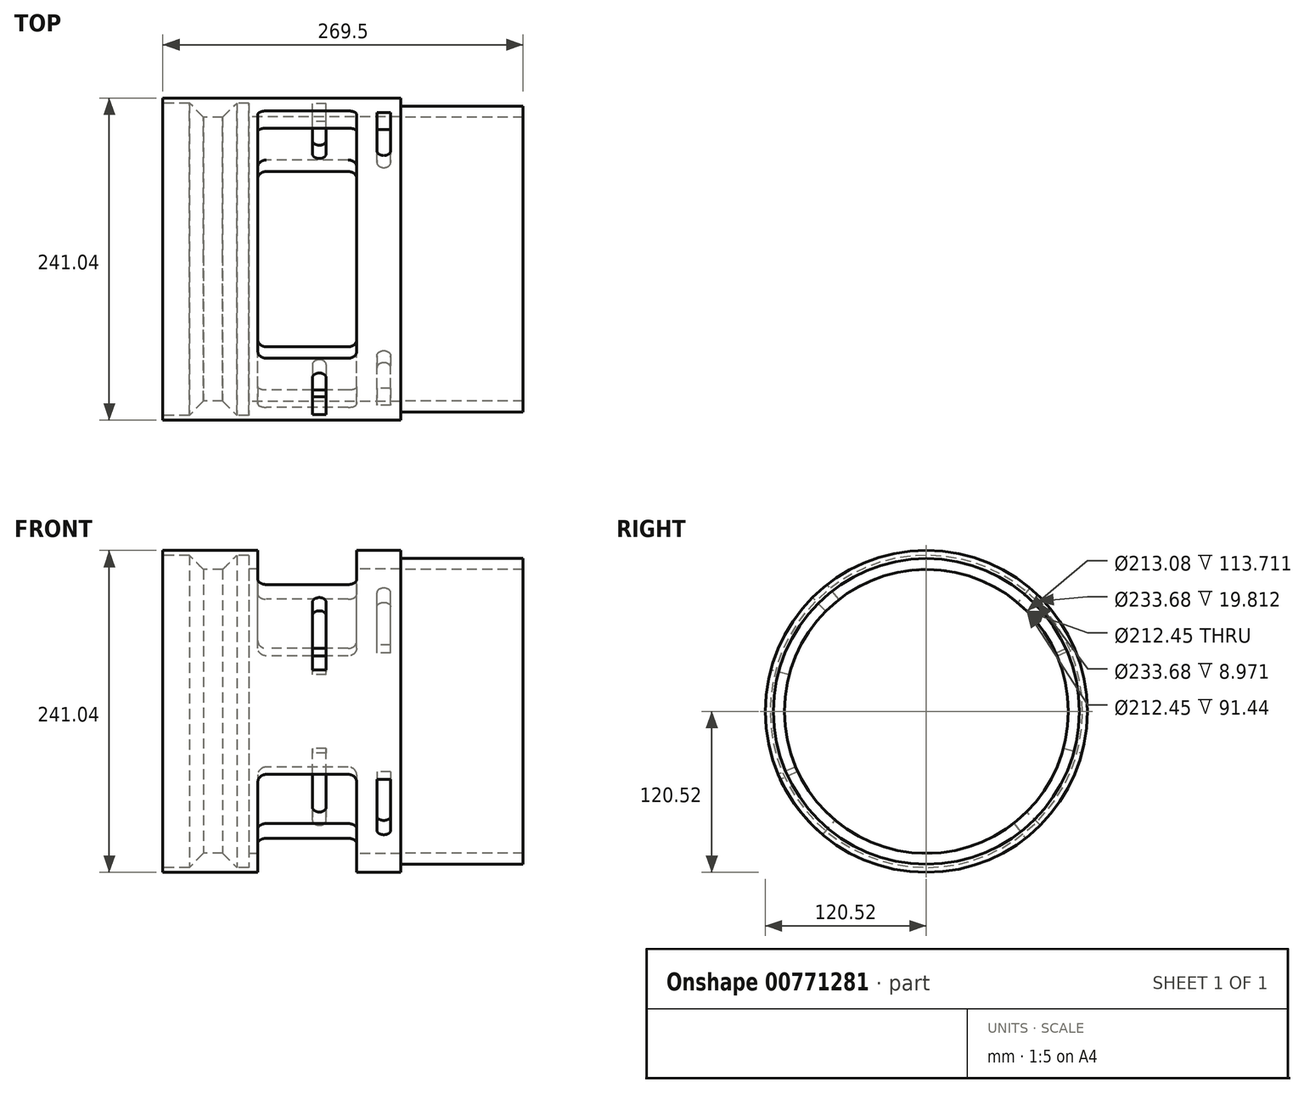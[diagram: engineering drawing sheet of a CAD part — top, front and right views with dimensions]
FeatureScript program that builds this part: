
annotation { "Feature Type Name" : "Feature", "Feature Type Description" : "" }
export const myFeature = defineFeature(function(context is Context, id is Id, definition is map)
    precondition{}
    {
        {
            var Q0;
            Q0=qCreatedBy(makeId("Front.planeOp"),FACE);
            var sketch = newSketch(context, id + "F0", { "sketchPlane" : qUnion([Q0])});
            skLineSegment(sketch, "E0", {"start": v(-108.05, 0) * mm, "end": v(161.45, 0) * mm, "construction": true});
            skLineSegment(sketch, "E1", {"start": v(-77.62, 106.22) * mm, "end": v(-63.3, 106.22) * mm});
            skLineSegment(sketch, "E2", {"start": v(-108.05, 116.84) * mm, "end": v(-108.05, 120.52) * mm});
            skLineSegment(sketch, "E3", {"start": v(-108.05, 120.52) * mm, "end": v(70, 120.52) * mm});
            skLineSegment(sketch, "E4", {"start": v(161.45, 114.44) * mm, "end": v(161.45, 106.22) * mm});
            skLineSegment(sketch, "E5", {"start": v(-108.05, 116.84) * mm, "end": v(-88.24, 116.84) * mm});
            skLineSegment(sketch, "E6", {"start": v(-88.24, 116.84) * mm, "end": v(-77.62, 106.22) * mm});
            skPoint(sketch, "E7.orphan", {"position": v(-108.05, 106.22) * mm});
            skLineSegment(sketch, "E8", {"start": v(70, 120.52) * mm, "end": v(70, 114.44) * mm});
            skLineSegment(sketch, "E9", {"start": v(70, 114.44) * mm, "end": v(161.45, 114.44) * mm});
            skLineSegment(sketch, "E10", {"start": v(-63.63, 105.89) * mm, "end": v(-52.68, 116.84) * mm});
            skLineSegment(sketch, "E11", {"start": v(-52.68, 116.84) * mm, "end": v(-43.7, 116.84) * mm});
            skLineSegment(sketch, "E12", {"start": v(-43.7, 116.84) * mm, "end": v(-43.7, 106.54) * mm});
            skLineSegment(sketch, "E13", {"start": v(-43.7, 106.54) * mm, "end": v(70, 106.54) * mm});
            skLineSegment(sketch, "E14", {"start": v(70, 106.54) * mm, "end": v(70, 106.22) * mm});
            skLineSegment(sketch, "E15.trimOffspring", {"start": v(70, 106.22) * mm, "end": v(161.45, 106.22) * mm});
            skSolve(sketch);
        }
        {
            var Q0;
            Q0 = qSketchRegion(id + "F0", true);
            var Q1;
            Q1=sQuery(id+"F0.wireOp",EDGE,"E0");
            revolve(context, id + "F1", {"surfaceOperationType" : NewSurfaceOperationType.NEW, "entities" : qUnion([Q0]), "axis" : qUnion([Q1]), "revolveType" : RevolveType.FULL});
        }
        {
            var Q0;
            Q0=qCreatedBy(makeId("Right.planeOp"),FACE);
            var sketch = newSketch(context, id + "F2", { "sketchPlane" : qUnion([Q0])});
            skLineSegment(sketch, "E16", {"start": v(0, 0) * mm, "end": v(-212.72, 0) * mm, "construction": true});
            skLineSegment(sketch, "E17", {"start": v(-60.07, 76.88) * mm, "end": v(-79.52, 101.78) * mm});
            skLineSegment(sketch, "E18", {"start": v(89.81, 38.12) * mm, "end": v(118.89, 50.47) * mm});
            skArc(sketch, "E19", {"start": v(89.81, 38.12) * mm, "mid": v(24.43, 94.46) * mm, "end": v(-60.07, 76.88) * mm});
            skArc(sketch, "E20", {"start": v(118.89, 50.47) * mm, "mid": v(32.34, 125.04) * mm, "end": v(-79.52, 101.78) * mm});
            skLineSegment(sketch, "E21", {"start": v(-89.81, -38.12) * mm, "end": v(-118.89, -50.47) * mm});
            skLineSegment(sketch, "E22", {"start": v(60.07, -76.88) * mm, "end": v(79.52, -101.78) * mm});
            skArc(sketch, "E23.trimOffspring", {"start": v(-89.81, -38.12) * mm, "mid": v(-24.43, -94.46) * mm, "end": v(60.07, -76.88) * mm});
            skArc(sketch, "E24.trimOffspring", {"start": v(-118.89, -50.47) * mm, "mid": v(-32.34, -125.04) * mm, "end": v(79.52, -101.78) * mm});
            skSolve(sketch);
        }
        {
            var Q0;
            Q0 = qSketchRegion(id + "F2", true);
            extrude(context, id + "F3", {"entities" : qUnion([Q0]), "operationType" : NewBodyOperationType.REMOVE, "endBound" : BoundingType.SYMMETRIC, "oppositeDirection" : true, "depth" : 73.9 * mm, "offsetDistance" : 25.4 * mm});
        }
        {
            var Q0;
            Q0=makeQuery(id+"F3.boolean.opBoolean","COPY",EDGE,{"derivedFrom":makeQuery(id+"F3.opExtrude","CAP_EDGE",EDGE,{"disambiguationData":[OSD([sQuery(id+"F2.wireOp",EDGE,"E17")])],"isStart":true})});
            var Q1;
            Q1=makeQuery(id+"F3.boolean.opBoolean","COPY",EDGE,{"derivedFrom":makeQuery(id+"F3.opExtrude","CAP_EDGE",EDGE,{"disambiguationData":[OSD([sQuery(id+"F2.wireOp",EDGE,"E17")])],"isStart":false})});
            var Q2;
            Q2=makeQuery(id+"F3.boolean.opBoolean","COPY",EDGE,{"derivedFrom":makeQuery(id+"F3.opExtrude","CAP_EDGE",EDGE,{"disambiguationData":[OSD([sQuery(id+"F2.wireOp",EDGE,"E18")])],"isStart":false})});
            var Q3;
            Q3=makeQuery(id+"F3.boolean.opBoolean","COPY",EDGE,{"derivedFrom":makeQuery(id+"F3.opExtrude","CAP_EDGE",EDGE,{"disambiguationData":[OSD([sQuery(id+"F2.wireOp",EDGE,"E18")])],"isStart":true})});
            var Q4;
            Q4=makeQuery(id+"F3.boolean.opBoolean","COPY",EDGE,{"derivedFrom":makeQuery(id+"F3.opExtrude","CAP_EDGE",EDGE,{"disambiguationData":[OSD([sQuery(id+"F2.wireOp",EDGE,"E21")])],"isStart":true})});
            var Q5;
            Q5=makeQuery(id+"F3.boolean.opBoolean","COPY",EDGE,{"derivedFrom":makeQuery(id+"F3.opExtrude","CAP_EDGE",EDGE,{"disambiguationData":[OSD([sQuery(id+"F2.wireOp",EDGE,"E22")])],"isStart":true})});
            var Q6;
            Q6=makeQuery(id+"F3.boolean.opBoolean","COPY",EDGE,{"derivedFrom":makeQuery(id+"F3.opExtrude","CAP_EDGE",EDGE,{"disambiguationData":[OSD([sQuery(id+"F2.wireOp",EDGE,"E21")])],"isStart":false})});
            var Q7;
            Q7=makeQuery(id+"F3.boolean.opBoolean","COPY",EDGE,{"derivedFrom":makeQuery(id+"F3.opExtrude","CAP_EDGE",EDGE,{"disambiguationData":[OSD([sQuery(id+"F2.wireOp",EDGE,"E22")])],"isStart":false})});
            fillet(context, id + "F4", {"entities" : qUnion([Q0, Q1, Q2, Q3, Q4, Q5, Q6, Q7]), "radius" : 6.35 * mm, "tangentPropagation" : true, "allowEdgeOverflow" : false});
        }
        {
            var Q0;
            Q0=qCreatedBy(makeId("Right.planeOp"),FACE);
            cPlane(context, id + "F5", {"entities" : qUnion([Q0]), "cplaneType" : CPlaneType.OFFSET, "offset" : 9.02 * mm, "width" : 152.4 * mm, "height" : 152.4 * mm});
        }
        {
            var Q0;
            Q0=qCreatedBy(id+"F5.planeOp",FACE);
            var sketch = newSketch(context, id + "F6", { "sketchPlane" : qUnion([Q0])});
            skLineSegment(sketch, "E25", {"start": v(68.72, -68.72) * mm, "end": v(90.36, -90.36) * mm});
            skArc(sketch, "E26", {"start": v(68.72, -68.72) * mm, "mid": v(84.17, -48.6) * mm, "end": v(93.88, -25.15) * mm});
            skArc(sketch, "E27", {"start": v(90.36, -90.36) * mm, "mid": v(110.67, -63.9) * mm, "end": v(123.43, -33.07) * mm});
            skLineSegment(sketch, "E28", {"start": v(-67.93, 67.93) * mm, "end": v(-89.43, 89.43) * mm});
            skArc(sketch, "E29", {"start": v(-67.93, 67.93) * mm, "mid": v(-83.2, 48.03) * mm, "end": v(-92.8, 24.86) * mm});
            skPoint(sketch, "E30.orphan", {"position": v(-87.22, 0) * mm});
            skArc(sketch, "E31.trimOffspring", {"start": v(-89.43, 89.43) * mm, "mid": v(-109.53, 63.24) * mm, "end": v(-122.16, 32.73) * mm});
            skLineSegment(sketch, "E32", {"start": v(-92.8, 24.86) * mm, "end": v(-122.16, 32.73) * mm});
            skLineSegment(sketch, "E33", {"start": v(93.88, -25.15) * mm, "end": v(123.43, -33.07) * mm});
            skSolve(sketch);
        }
        {
            var Q0;
            Q0 = qSketchRegion(id + "F6", true);
            extrude(context, id + "F7", {"entities" : qUnion([Q0]), "operationType" : NewBodyOperationType.REMOVE, "endBound" : BoundingType.SYMMETRIC, "oppositeDirection" : true, "depth" : 10.3 * mm, "offsetDistance" : 25.4 * mm});
        }
        {
            var Q0;
            Q0=makeQuery(id+"F7.boolean.opBoolean","COPY",EDGE,{"derivedFrom":makeQuery(id+"F7.opExtrude","CAP_EDGE",EDGE,{"disambiguationData":[OSD([sQuery(id+"F6.wireOp",EDGE,"E25")])],"isStart":true})});
            var Q1;
            Q1=makeQuery(id+"F7.boolean.opBoolean","COPY",EDGE,{"derivedFrom":makeQuery(id+"F7.opExtrude","CAP_EDGE",EDGE,{"disambiguationData":[OSD([sQuery(id+"F6.wireOp",EDGE,"E25")])],"isStart":false})});
            var Q2;
            Q2=makeQuery(id+"F7.boolean.opBoolean","COPY",EDGE,{"derivedFrom":makeQuery(id+"F7.opExtrude","CAP_EDGE",EDGE,{"disambiguationData":[OSD([sQuery(id+"F6.wireOp",EDGE,"E28")])],"isStart":false})});
            var Q3;
            Q3=makeQuery(id+"F7.boolean.opBoolean","COPY",EDGE,{"derivedFrom":makeQuery(id+"F7.opExtrude","CAP_EDGE",EDGE,{"disambiguationData":[OSD([sQuery(id+"F6.wireOp",EDGE,"E28")])],"isStart":true})});
            fillet(context, id + "F8", {"entities" : qUnion([Q0, Q1, Q2, Q3]), "radius" : 5.16 * mm, "tangentPropagation" : true, "allowEdgeOverflow" : false});
        }
        {
            var Q0;
            Q0=qCreatedBy(id+"F5.planeOp",FACE);
            cPlane(context, id + "F9", {"entities" : qUnion([Q0]), "cplaneType" : CPlaneType.OFFSET, "offset" : 48.26 * mm, "width" : 152.4 * mm, "height" : 152.4 * mm});
        }
        {
            var Q0;
            Q0=qCreatedBy(id+"F9.planeOp",FACE);
            var sketch = newSketch(context, id + "F10", { "sketchPlane" : qUnion([Q0])});
            skLineSegment(sketch, "E34", {"start": v(91.92, 41.32) * mm, "end": v(115.07, 52.12) * mm});
            skLineSegment(sketch, "E35", {"start": v(64.78, 77.2) * mm, "end": v(81.2, 96.77) * mm});
            skArc(sketch, "E36", {"start": v(115.07, 52.12) * mm, "mid": v(100.64, 76.34) * mm, "end": v(81.2, 96.77) * mm});
            skArc(sketch, "E37", {"start": v(91.92, 41.32) * mm, "mid": v(80.38, 60.8) * mm, "end": v(64.78, 77.2) * mm});
            skPoint(sketch, "E38.orphan", {"position": v(3.3, 0) * mm});
            skLineSegment(sketch, "E39", {"start": v(-87.63, -40.86) * mm, "end": v(-116.68, -54.4) * mm});
            skLineSegment(sketch, "E40", {"start": v(-62.15, -74.07) * mm, "end": v(-82.75, -98.62) * mm});
            skArc(sketch, "E41", {"start": v(-87.63, -40.86) * mm, "mid": v(-76.7, -58.86) * mm, "end": v(-62.15, -74.07) * mm});
            skArc(sketch, "E42", {"start": v(-116.68, -54.4) * mm, "mid": v(-102.14, -78.37) * mm, "end": v(-82.75, -98.62) * mm});
            skSolve(sketch);
        }
        {
            var Q0;
            Q0 = qSketchRegion(id + "F10", true);
            extrude(context, id + "F11", {"entities" : qUnion([Q0]), "operationType" : NewBodyOperationType.REMOVE, "endBound" : BoundingType.SYMMETRIC, "depth" : 10.3 * mm, "offsetDistance" : 25.4 * mm});
        }
        {
            var Q0;
            Q0=makeQuery(id+"F11.boolean.opBoolean","COPY",EDGE,{"derivedFrom":makeQuery(id+"F11.opExtrude","CAP_EDGE",EDGE,{"disambiguationData":[OSD([sQuery(id+"F10.wireOp",EDGE,"E35")])],"isStart":false})});
            var Q1;
            Q1=makeQuery(id+"F11.boolean.opBoolean","COPY",EDGE,{"derivedFrom":makeQuery(id+"F11.opExtrude","CAP_EDGE",EDGE,{"disambiguationData":[OSD([sQuery(id+"F10.wireOp",EDGE,"E35")])],"isStart":true})});
            var Q2;
            Q2=makeQuery(id+"F11.boolean.opBoolean","COPY",EDGE,{"derivedFrom":makeQuery(id+"F11.opExtrude","CAP_EDGE",EDGE,{"disambiguationData":[OSD([sQuery(id+"F10.wireOp",EDGE,"E40")])],"isStart":false})});
            var Q3;
            Q3=makeQuery(id+"F11.boolean.opBoolean","COPY",EDGE,{"derivedFrom":makeQuery(id+"F11.opExtrude","CAP_EDGE",EDGE,{"disambiguationData":[OSD([sQuery(id+"F10.wireOp",EDGE,"E40")])],"isStart":true})});
            fillet(context, id + "F12", {"entities" : qUnion([Q0, Q1, Q2, Q3]), "radius" : 5.16 * mm, "tangentPropagation" : true, "allowEdgeOverflow" : false});
        }
    });
